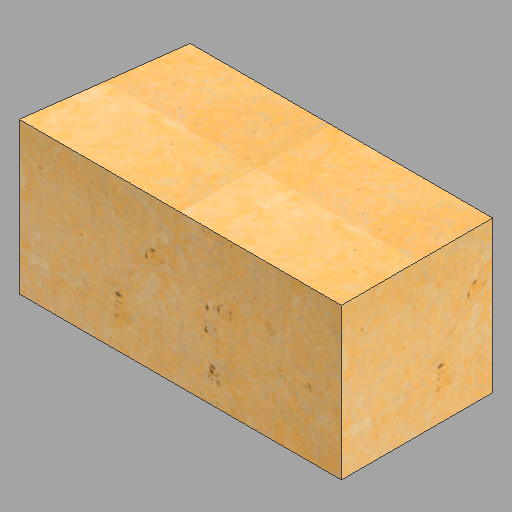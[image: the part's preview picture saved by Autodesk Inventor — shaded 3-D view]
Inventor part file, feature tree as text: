
AUTODESK INVENTOR PART (.ipt)
format: ipt  version: 2023 (Build 270158000, 158)  size: 386,048 bytes
history: native  units: in
note: dims shown in document units (in); Inventor stores cm internally (conversion verified against a paired STEP export)
features: other x1, extrude x1, sketch x1
ambient origin geometry x8: Origin, YZ Plane, XZ Plane, XY Plane, X Axis, Y Axis, Z Axis, Center Point
bodies: Solid1 (feature_tree)
feature tree (3):
  other  "B - 2"
  extrude  "Extrusion1"  Depth=24.0in
  sketch  "Sketch1"  dims[d0=48.0in d1=24.0in d2=51.125in d3=24.0in d4=0.0in]
